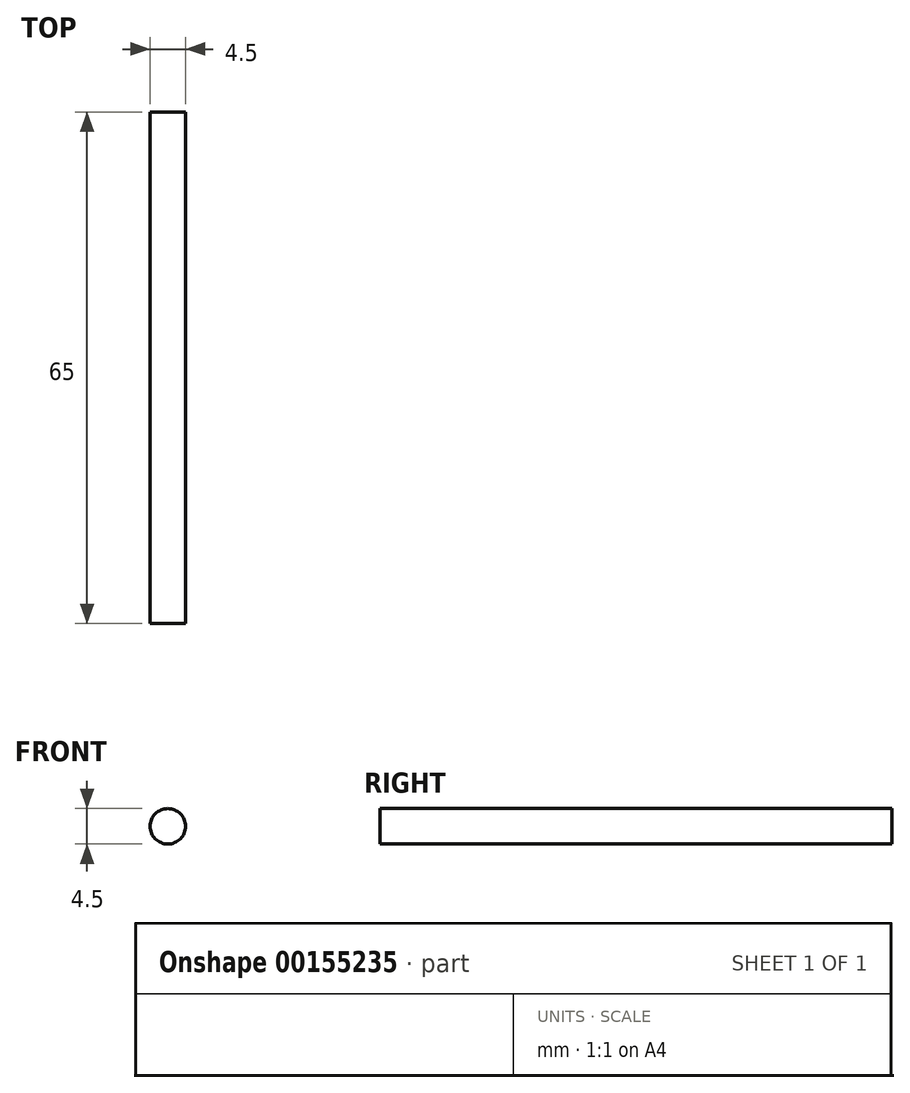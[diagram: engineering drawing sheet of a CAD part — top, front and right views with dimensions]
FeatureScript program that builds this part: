
annotation { "Feature Type Name" : "Feature", "Feature Type Description" : "" }
export const myFeature = defineFeature(function(context is Context, id is Id, definition is map)
    precondition{}
    {
        {
            var Q0;
            Q0=qCreatedBy(makeId("Front.planeOp"),FACE);
            var sketch = newSketch(context, id + "F0", { "sketchPlane" : qUnion([Q0])});
            skCircle(sketch, "E0", {"center": v(0, 0) * mm, "radius": 2.25 * mm});
            skSolve(sketch);
        }
        {
            var Q0;
            Q0 = qSketchRegion(id + "F0", true);
            extrude(context, id + "F1", {"entities" : qUnion([Q0]), "depth" : 65 * mm});
        }
    });
